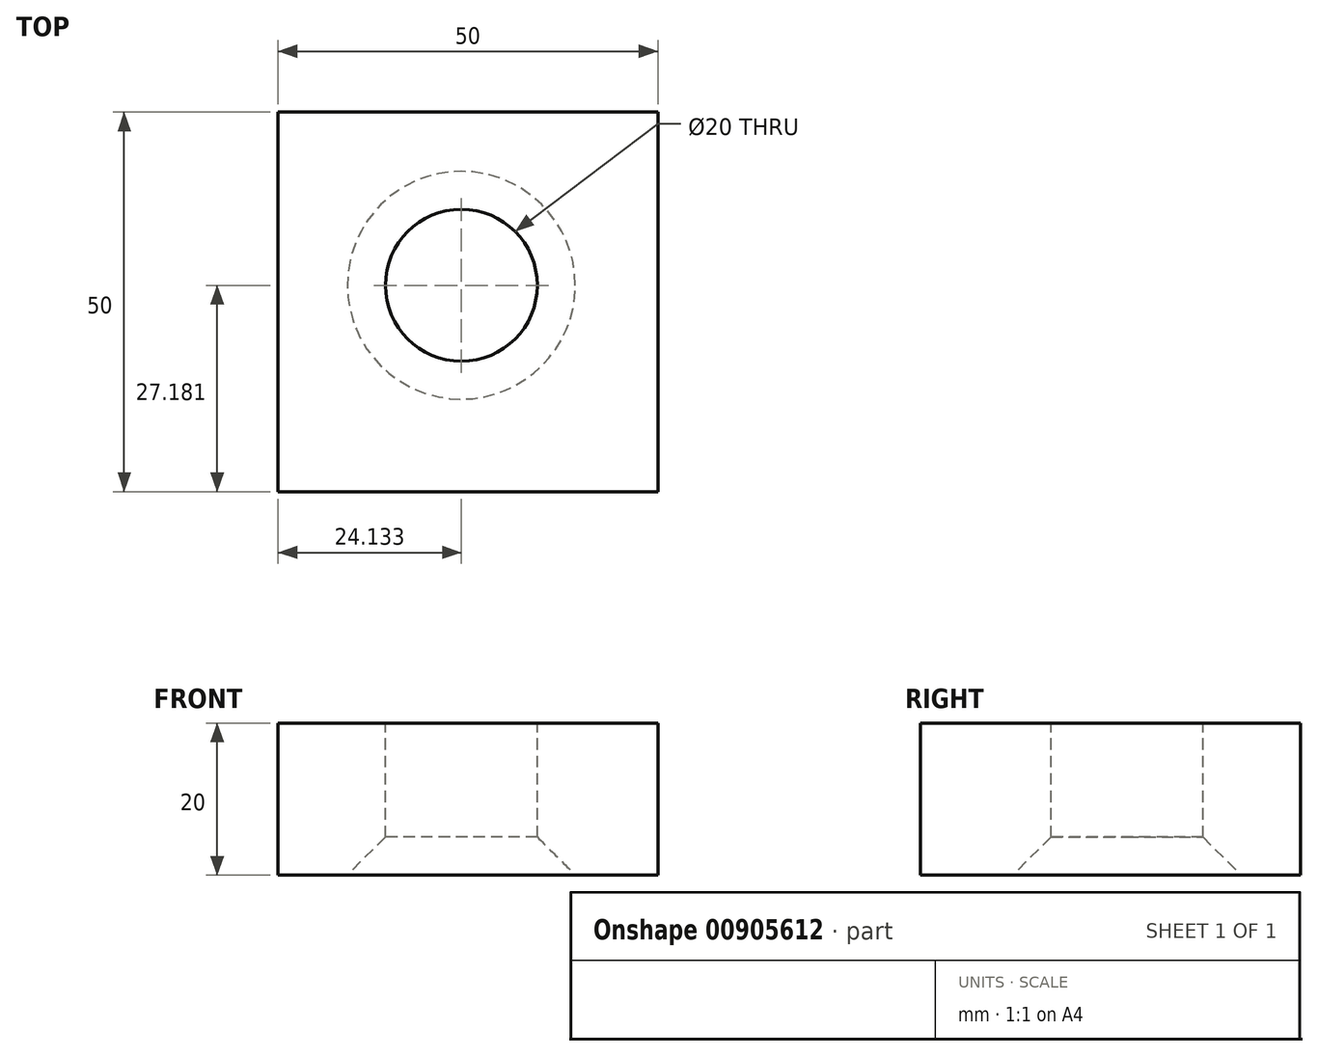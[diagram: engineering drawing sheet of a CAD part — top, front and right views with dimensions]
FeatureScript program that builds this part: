
annotation { "Feature Type Name" : "Feature", "Feature Type Description" : "" }
export const myFeature = defineFeature(function(context is Context, id is Id, definition is map)
    precondition{}
    {
        {
            var Q0;
            Q0=qCreatedBy(makeId("Top.planeOp"),FACE);
            var sketch = newSketch(context, id + "F0", { "sketchPlane" : qUnion([Q0])});
            skLineSegment(sketch, "E0.bottom", {"start": v(0, 0) * mm, "end": v(50, 0) * mm});
            skLineSegment(sketch, "E0.top", {"start": v(0, 50) * mm, "end": v(50, 50) * mm});
            skLineSegment(sketch, "E0.left", {"start": v(0, 0) * mm, "end": v(0, 50) * mm});
            skLineSegment(sketch, "E0.right", {"start": v(50, 0) * mm, "end": v(50, 50) * mm});
            skSolve(sketch);
        }
        {
            var Q0;
            Q0 = qSketchRegion(id + "F0", true);
            extrude(context, id + "F1", {"entities" : qUnion([Q0]), "depth" : 20 * mm, "offsetDistance" : 25 * mm});
        }
        {
            var Q0;
            Q0=makeQuery(id+"F1.opExtrude","CAP_FACE",FACE,{"disambiguationData":[OSD([sQuery(id+"F0.wireOp",EDGE,"E0.bottom"),sQuery(id+"F0.wireOp",EDGE,"E0.top"),sQuery(id+"F0.wireOp",EDGE,"E0.left"),sQuery(id+"F0.wireOp",EDGE,"E0.right")])],"isStart":false});
            var sketch = newSketch(context, id + "F2", { "sketchPlane" : qUnion([Q0])});
            skCircle(sketch, "E1", {"center": v(24.13, 27.18) * mm, "radius": 10 * mm});
            skSolve(sketch);
        }
        {
            var Q0;
            Q0 = qSketchRegion(id + "F2", true);
            extrude(context, id + "F3", {"entities" : qUnion([Q0]), "operationType" : NewBodyOperationType.REMOVE, "oppositeDirection" : true, "depth" : 25 * mm, "offsetDistance" : 25 * mm});
        }
        {
            var Q0;
            Q0=makeQuery(id+"F3.boolean.opBoolean","COPY",EDGE,{"derivedFrom":makeQuery(id+"F3.opExtrude","CAP_EDGE",EDGE,{"disambiguationData":[OSD([sQuery(id+"F2.wireOp",EDGE,"E1")])],"isStart":true})});
            var Q1;
            Q1=makeQuery(id+"F3.boolean.opBoolean","INTERSECT",EDGE,{"derivedFrom":[makeQuery(id+"F1.opExtrude","CAP_FACE",FACE,{"disambiguationData":[OSD([sQuery(id+"F0.wireOp",EDGE,"E0.bottom"),sQuery(id+"F0.wireOp",EDGE,"E0.top"),sQuery(id+"F0.wireOp",EDGE,"E0.left"),sQuery(id+"F0.wireOp",EDGE,"E0.right")])],"isStart":true}),makeQuery(id+"F3.opExtrude","SWEPT_FACE",FACE,{"disambiguationData":[OSD([sQuery(id+"F2.wireOp",EDGE,"E1")])]})]});
            chamfer(context, id + "F4", {"entities" : qUnion([Q0, Q1]), "width" : 5 * mm, "tangentPropagation" : true});
        }
    });
